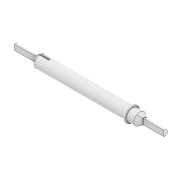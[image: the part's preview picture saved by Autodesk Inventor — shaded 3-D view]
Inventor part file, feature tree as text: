
AUTODESK INVENTOR PART (.ipt)
format: ipt  version: 2022 (Build 260153000, 153)  size: 207,872 bytes
history: native  units: mm
features: extrude x4, sketch x4, plane x3, thicken_offset x2, projected_geometry x2, other x2, loft x1, fillet x1, mirror x1
ambient origin geometry x8: Origin, YZ Plane, XZ Plane, XY Plane, X Axis, Y Axis, Z Axis, Center Point
bodies: Solid1 (feature_tree)
feature tree (20):
  extrude  "Shaft"  Depth=10.0mm TaperAngle=0.0deg
  plane  "Work Plane1"
  extrude  "Wheel Insert Profile"  Depth=7.5mm
  thicken_offset  "Thicken5"
  loft  "Loft1"
  plane  "Work Plane2"
  extrude  "Stopper"  Depth=2.0mm
  fillet  "Fillet1"  [1 undecoded]
  mirror  "Mirror1"
  plane  "Work Plane5"
  extrude  "Extrusion7"  Depth=0.15mm
  thicken_offset  "Thicken6"
  sketch  "Sketch1"  dims[d2=0.0mm d25=10.0mm d26=0.0mm]
  sketch  "Sketch3"  dims[d29=2.0mm d32=0.0mm d33=90.0deg d35=7.5mm]
  sketch  "Sketch4"  dims[d36=1.0mm d37=0.0mm d38=0.5mm]
  projected_geometry  "Projected Loop1"
  other  "Edges2"
  other  "Edges6"
  sketch  "Sketch10"  dims[d89=3.0mm d90=2.0mm d91=0.0mm d92=90.0deg d93=0.15mm d94=0.15mm d95=0.5mm d96=0.5mm d97=0.0mm d98=0.0mm d99=0.1mm d100=0.1mm d101=-15.5mm d102=-16.5mm d103=0.5mm d104=0.5mm]
  projected_geometry  "Project Cut Edges3"
note: 1 required parameter value undecoded (feature->parameter linkage not recoverable at this tier; creation-order binding heuristic only, values carry confidence <= 0.55)
